# Revit family: QF_MACOM_CAB-2A
name_source: partatom
category: Equipamento especial
units: mm (PartAtom-declared; Revit-internal decimal feet)

## family parameters
Com base no plano de trabalho = Não
Compartilhado = Não
Corte com vazios quando carregada = Não
Cota do conector redondo = Utilizar diâmetro
Número OmniClass = 23.40.40.11.11.11
Ponto de cálculo do ambiente = Não
Sempre na vertical = Sim
Tipo de parte = Normal
Título OmniClass = Refrigerators

## types (1)
- CAB-2A
    Cycle = 60 Hz
    Depth = 420 mm
    Descrição = CABECOTE REFRIGERADO MACOM PARA 05 GN 1/3-150 COM 5 SUPORTES INTERNOS E PÉS 180mm
    Elec Connection Height = 207 mm
    Electric Power = 307 W
    Elevação padrão = 0 mm
    Fabricante = MACOM
    Height = 440 mm
    Ingress Protection Code = IP 22
    Modelo = CAB-2A
    Operational Current = 2 A
    Refrigeration Climate Class = 4
    Refrigerent Type = R134a
    Show Clearances = Sim
    Show Logo = Sim
    URL = https://www.acosmacom.com.br
    Volts = 220 V
    Volume = 0,14 m³
    Weight = 69,00 kg
    Width = 1380 mm
    Work Temperature = -4 ºC to +5 ºC

## geometry (parser evidence)
native form markers: Sweep x14
no freeform markers — native parametric forms only
